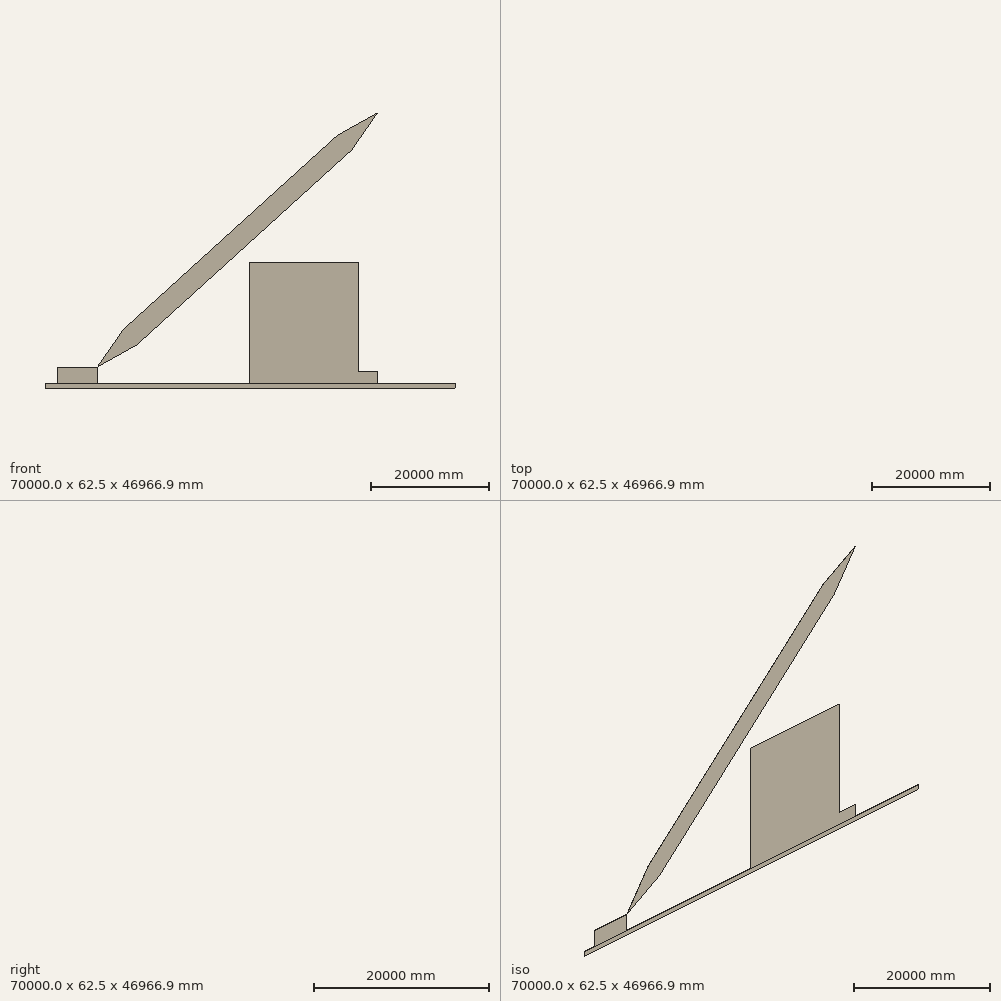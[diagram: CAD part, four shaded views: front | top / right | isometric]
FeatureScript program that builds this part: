
annotation { "Feature Type Name" : "Feature", "Feature Type Description" : "" }
export const myFeature = defineFeature(function(context is Context, id is Id, definition is map)
    precondition{}
    {
        {
            var Q0;
            Q0=qCreatedBy(makeId("Front.planeOp"),FACE);
            var sketch = newSketch(context, id + "F0", { "sketchPlane" : qUnion([Q0])});
            skLineSegment(sketch, "E0.bottom", {"start": v(35000, -400) * mm, "end": v(-35000, -400) * mm});
            skLineSegment(sketch, "E0.top", {"start": v(35000, 400) * mm, "end": v(-35000, 400) * mm});
            skLineSegment(sketch, "E0.left", {"start": v(35000, -400) * mm, "end": v(35000, 400) * mm});
            skLineSegment(sketch, "E0.right", {"start": v(-35000, -400) * mm, "end": v(-35000, 400) * mm});
            skPoint(sketch, "E0.middle", {"position": v(0, 0) * mm});
            skSolve(sketch);
        }
        {
            var Q0;
            Q0=makeQuery(id+"F0.imprint","IMPRINT",FACE,{"disambiguationData":[TD([[makeQuery(id+"F0.imprint","IMPRINT",EDGE,{"derivedFrom":sQuery(id+"F0.wireOp",EDGE,"E0.bottom")}),-1.0]])]});
            extrude(context, id + "F1", {"entities" : qUnion([Q0]), "endBound" : BoundingType.SYMMETRIC, "depth" : 25 * mm, "offsetDistance" : 25 * mm});
        }
        {
            var Q0;
            Q0=makeQuery(id+"F1.opExtrude","CAP_FACE",FACE,{"disambiguationData":[OSD([sQuery(id+"F0.wireOp",EDGE,"E0.bottom"),sQuery(id+"F0.wireOp",EDGE,"E0.top"),sQuery(id+"F0.wireOp",EDGE,"E0.left"),sQuery(id+"F0.wireOp",EDGE,"E0.right")])],"isStart":false});
            var sketch = newSketch(context, id + "F2", { "sketchPlane" : qUnion([Q0])});
            skLineSegment(sketch, "E1.bottom", {"start": v(-33000, 400) * mm, "end": v(-26130, 400) * mm});
            skLineSegment(sketch, "E1.top", {"start": v(-33000, 3158) * mm, "end": v(-26130, 3158) * mm});
            skLineSegment(sketch, "E1.left", {"start": v(-33000, 400) * mm, "end": v(-33000, 3158) * mm});
            skLineSegment(sketch, "E1.right", {"start": v(-26130, 400) * mm, "end": v(-26130, 3158) * mm});
            skSolve(sketch);
        }
        {
            var Q0;
            Q0 = qSketchRegion(id + "F2", true);
            extrude(context, id + "F3", {"entities" : qUnion([Q0]), "depth" : 25 * mm, "offsetDistance" : 25 * mm});
        }
        {
            var Q0;
            Q0=makeQuery(id+"F1.opExtrude","CAP_FACE",FACE,{"disambiguationData":[OSD([sQuery(id+"F0.wireOp",EDGE,"E0.bottom"),sQuery(id+"F0.wireOp",EDGE,"E0.top"),sQuery(id+"F0.wireOp",EDGE,"E0.left"),sQuery(id+"F0.wireOp",EDGE,"E0.right")])],"isStart":false});
            var sketch = newSketch(context, id + "F4", { "sketchPlane" : qUnion([Q0])});
            skLineSegment(sketch, "E2.bottom", {"start": v(-130, 400) * mm, "end": v(18435, 400) * mm});
            skLineSegment(sketch, "E2.top", {"start": v(-130, 21000) * mm, "end": v(18435, 21000) * mm});
            skLineSegment(sketch, "E2.left", {"start": v(-130, 400) * mm, "end": v(-130, 21000) * mm});
            skLineSegment(sketch, "E2.right", {"start": v(18435, 400) * mm, "end": v(18435, 21000) * mm});
            skLineSegment(sketch, "E3.bottom", {"start": v(18435, 2400) * mm, "end": v(21735, 2400) * mm});
            skLineSegment(sketch, "E3.top", {"start": v(18435, 400) * mm, "end": v(21735, 400) * mm});
            skLineSegment(sketch, "E3.left", {"start": v(18435, 2400) * mm, "end": v(18435, 400) * mm});
            skLineSegment(sketch, "E3.right", {"start": v(21735, 2400) * mm, "end": v(21735, 400) * mm});
            skSolve(sketch);
        }
        {
            var Q0;
            Q0 = qSketchRegion(id + "F4", true);
            extrude(context, id + "F5", {"entities" : qUnion([Q0]), "operationType" : NewBodyOperationType.ADD, "endBound" : BoundingType.SYMMETRIC, "depth" : 25 * mm, "offsetDistance" : 25 * mm});
        }
        {
            var Q0;
            Q0=makeQuery(id+"F3.opExtrude","CAP_FACE",FACE,{"disambiguationData":[OSD([sQuery(id+"F2.wireOp",EDGE,"E1.bottom"),sQuery(id+"F2.wireOp",EDGE,"E1.top"),sQuery(id+"F2.wireOp",EDGE,"E1.left"),sQuery(id+"F2.wireOp",EDGE,"E1.right")])],"isStart":false});
            var sketch = newSketch(context, id + "F6", { "sketchPlane" : qUnion([Q0])});
            skLineSegment(sketch, "E4", {"start": v(-26130, 3158) * mm, "end": v(21735, 46566.87) * mm, "construction": true});
            skLineSegment(sketch, "E5", {"start": v(21735, 46566.87) * mm, "end": v(21735, 1400) * mm});
            skLineSegment(sketch, "E6", {"start": v(-26130, 3158) * mm, "end": v(-21661.13, 9573.3) * mm});
            skLineSegment(sketch, "E7", {"start": v(-21661.13, 9573.3) * mm, "end": v(-19309.89, 6980.7) * mm, "construction": true});
            skLineSegment(sketch, "E8", {"start": v(-19309.89, 6980.7) * mm, "end": v(-26130, 3158) * mm});
            skLineSegment(sketch, "E9", {"start": v(21735, 46566.87) * mm, "end": v(14914.89, 42744.18) * mm});
            skLineSegment(sketch, "E10", {"start": v(14914.89, 42744.18) * mm, "end": v(17266.13, 40151.56) * mm, "construction": true});
            skLineSegment(sketch, "E11", {"start": v(17266.13, 40151.56) * mm, "end": v(21735, 46566.87) * mm});
            skLineSegment(sketch, "E12", {"start": v(17266.13, 40151.56) * mm, "end": v(-19309.89, 6980.7) * mm});
            skLineSegment(sketch, "E13", {"start": v(-21661.13, 9573.3) * mm, "end": v(14914.89, 42744.18) * mm});
            skSolve(sketch);
        }
        {
            var Q0;
            Q0=makeQuery(id+"F6.imprint","IMPRINT",FACE,{"disambiguationData":[TD([[makeQuery(id+"F6.imprint","IMPRINT",EDGE,{"derivedFrom":sQuery(id+"F6.wireOp",EDGE,"E6")}),-1.0]])]});
            extrude(context, id + "F7", {"entities" : qUnion([Q0]), "endBound" : BoundingType.SYMMETRIC, "depth" : 25 * mm, "offsetDistance" : 25 * mm});
        }
    });
